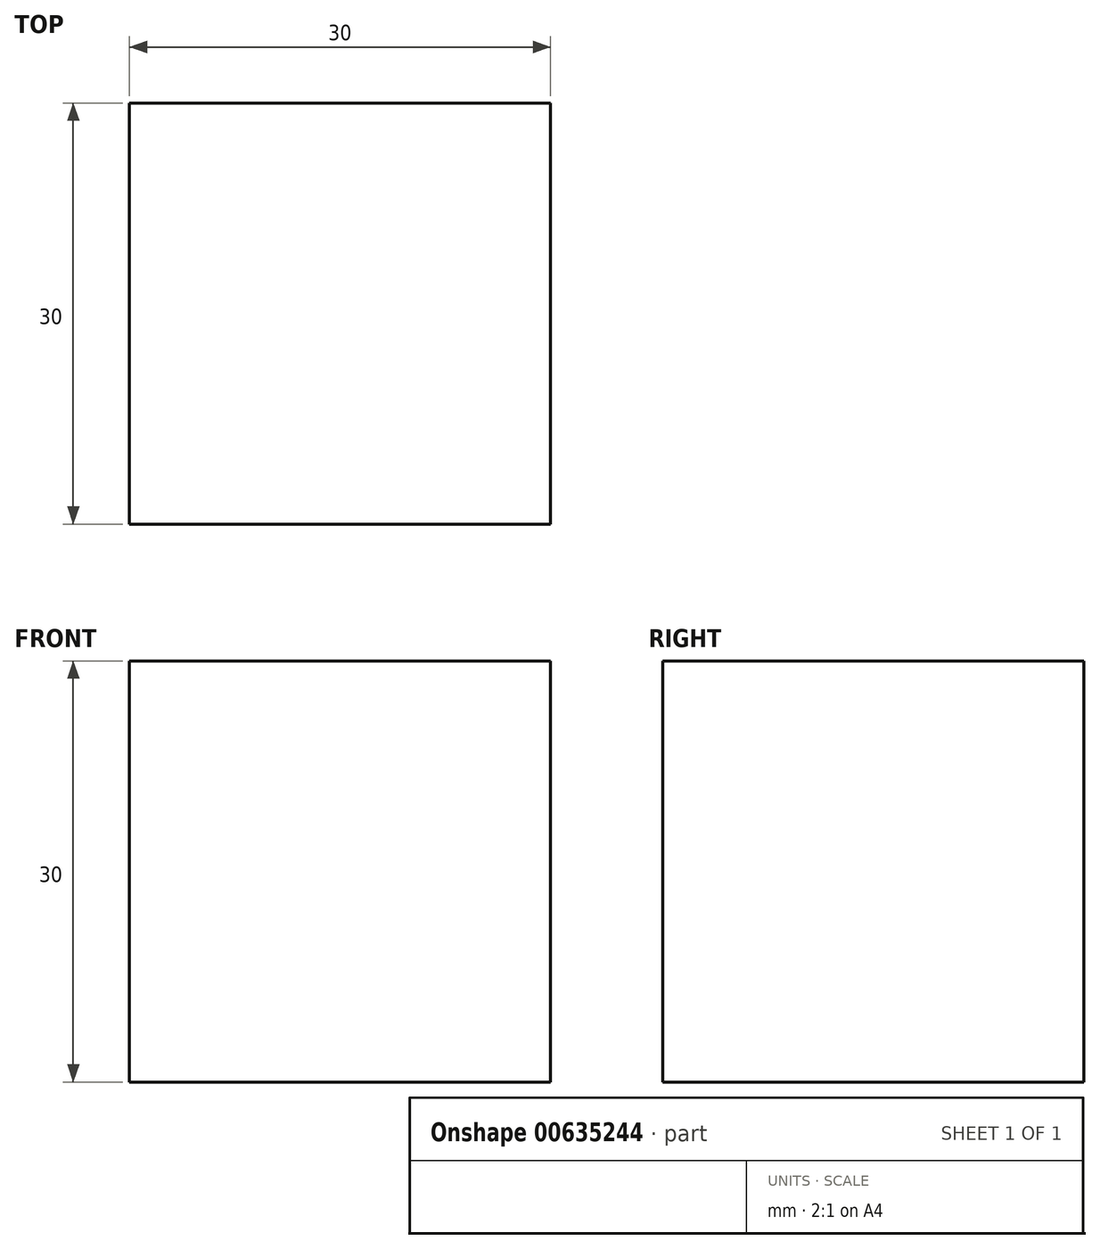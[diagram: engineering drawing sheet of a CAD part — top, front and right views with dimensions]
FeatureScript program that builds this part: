
annotation { "Feature Type Name" : "Feature", "Feature Type Description" : "" }
export const myFeature = defineFeature(function(context is Context, id is Id, definition is map)
    precondition{}
    {
        {
            var Q0;
            Q0=qCreatedBy(makeId("Top.planeOp"),FACE);
            var sketch = newSketch(context, id + "F0", { "sketchPlane" : qUnion([Q0])});
            skLineSegment(sketch, "E0.bottom", {"start": v(-15, 15) * mm, "end": v(15, 15) * mm});
            skLineSegment(sketch, "E0.top", {"start": v(-15, -15) * mm, "end": v(15, -15) * mm});
            skLineSegment(sketch, "E0.left", {"start": v(-15, 15) * mm, "end": v(-15, -15) * mm});
            skLineSegment(sketch, "E0.right", {"start": v(15, 15) * mm, "end": v(15, -15) * mm});
            skSolve(sketch);
        }
        {
            var Q0;
            Q0=makeQuery(id+"F0.imprint","IMPRINT",FACE,{"disambiguationData":[TD([[makeQuery(id+"F0.imprint","IMPRINT",EDGE,{"derivedFrom":sQuery(id+"F0.wireOp",EDGE,"HNTWVaQk-ma07-HCja-nrTM-6IoCofefVgxw")}),1.0]])]});
            var Q1;
            Q1=makeQuery(id+"F0.imprint","IMPRINT",FACE,{"disambiguationData":[TD([[makeQuery(id+"F0.imprint","IMPRINT",EDGE,{"derivedFrom":sQuery(id+"F0.wireOp",EDGE,"E0.bottom")}),-1.0]])]});
            extrude(context, id + "F1", {"entities" : qUnion([Q0, Q1]), "depth" : 30 * mm, "offsetDistance" : 25 * mm});
        }
    });
